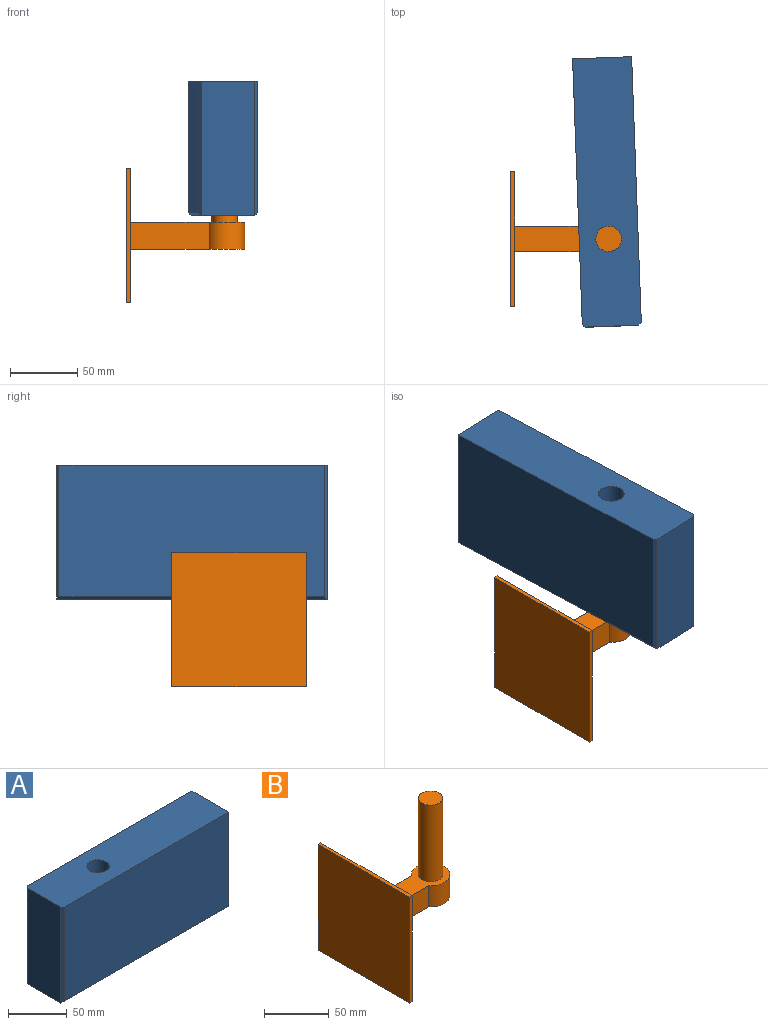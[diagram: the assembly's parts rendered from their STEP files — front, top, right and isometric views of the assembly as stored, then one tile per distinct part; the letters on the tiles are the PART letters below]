
ASSEMBLY  parts=2 mates=1
PART A: 11 faces, bbox 200x44x100 mm
  f0: plane 100x40mm, normal (-1,0,0), area 4000mm2, adj f5,f6,f8,f10
  f1: plane 198x98mm, normal (0,-1,0), area 19404mm2, adj f2,f5,f9,f10
  f2: plane 100x44mm, normal (1,0,0), area 4396mm2, adj f1,f3,f5,f6,f7,f9
  f3: plane 198x98mm, normal (0,1,0), area 19404mm2, adj f2,f5,f7,f8
  f4: cylinder r=9.5mm len=100mm, axis (0,0,-1), area 5969mm2, adj f5,f6
  f5: plane 200x44mm, normal (0,0,1), area 8512.5mm2, adj f0,f1,f2,f3,f4,f8,f10
  f6: plane 200x40mm, normal (0,0,-1), area 7716.5mm2, adj f0,f2,f4,f7,f9
  f7: plane 200x2mm, normal (0,0.71,-0.71), area 562.9mm2, adj f2,f3,f6,f8
  f8: plane 100x2mm, normal (-0.71,0.71,0), area 280mm2, adj f0,f3,f5,f7
  f9: plane 200x2mm, normal (0,-0.71,-0.71), area 562.9mm2, adj f1,f2,f6,f10
  f10: plane 100x2mm, normal (-0.71,-0.71,0), area 280mm2, adj f0,f1,f5,f9
PART B: 13 faces, bbox 88x100x132.5 mm
  f0: plane 100x100mm, normal (1,0,0), area 9620mm2, adj f1,f3,f4,f5,f6,f8,f9,f10
  f1: plane 100x3mm, normal (0,1,0), area 300mm2, adj f0,f2,f4,f5
  f2: plane 100x100mm, normal (-1,0,0), area 10000mm2, adj f1,f3,f4,f5
  f3: plane 100x3mm, normal (0,-1,0), area 300mm2, adj f0,f2,f4,f5
  f4: plane 100x3mm, normal (0,0,1), area 300mm2, adj f0,f1,f2,f3
  f5: plane 100x3mm, normal (0,0,-1), area 300mm2, adj f0,f1,f2,f3
  f6: plane 58.39x20mm, normal (0,-1,0), area 1167.8mm2, adj f0,f7,f9,f10
  f7: cylinder r=15mm len=30mm, axis (0,0,-1), area 1473.4mm2, adj f6,f8,f9,f10
  f8: plane 58.39x20mm, normal (0,1,0), area 1167.8mm2, adj f0,f7,f9,f10
  f9: plane 85x30mm, normal (0,0,1), area 1488.7mm2, adj f0,f6,f7,f8,f11
  f10: plane 85x30mm, normal (0,0,-1), area 1772.3mm2, adj f0,f6,f7,f8
  f11: cylinder r=9.5mm len=72.5mm, axis (0,0,-1), area 4327.5mm2, adj f9,f12
  f12: plane 19x19mm, normal (0,0,1), area 283.5mm2, adj f11
PLACE A rot(axis=(0,0,1),92.1deg) t=(-35.22,19.52,-6.4)mm
PLACE B t=(-35.22,19.52,-21.4)mm
MATE cylindrical A.f4 <-> B.f11  axis (0,0,-1) through (-35.22,19.52,-6.4)mm
